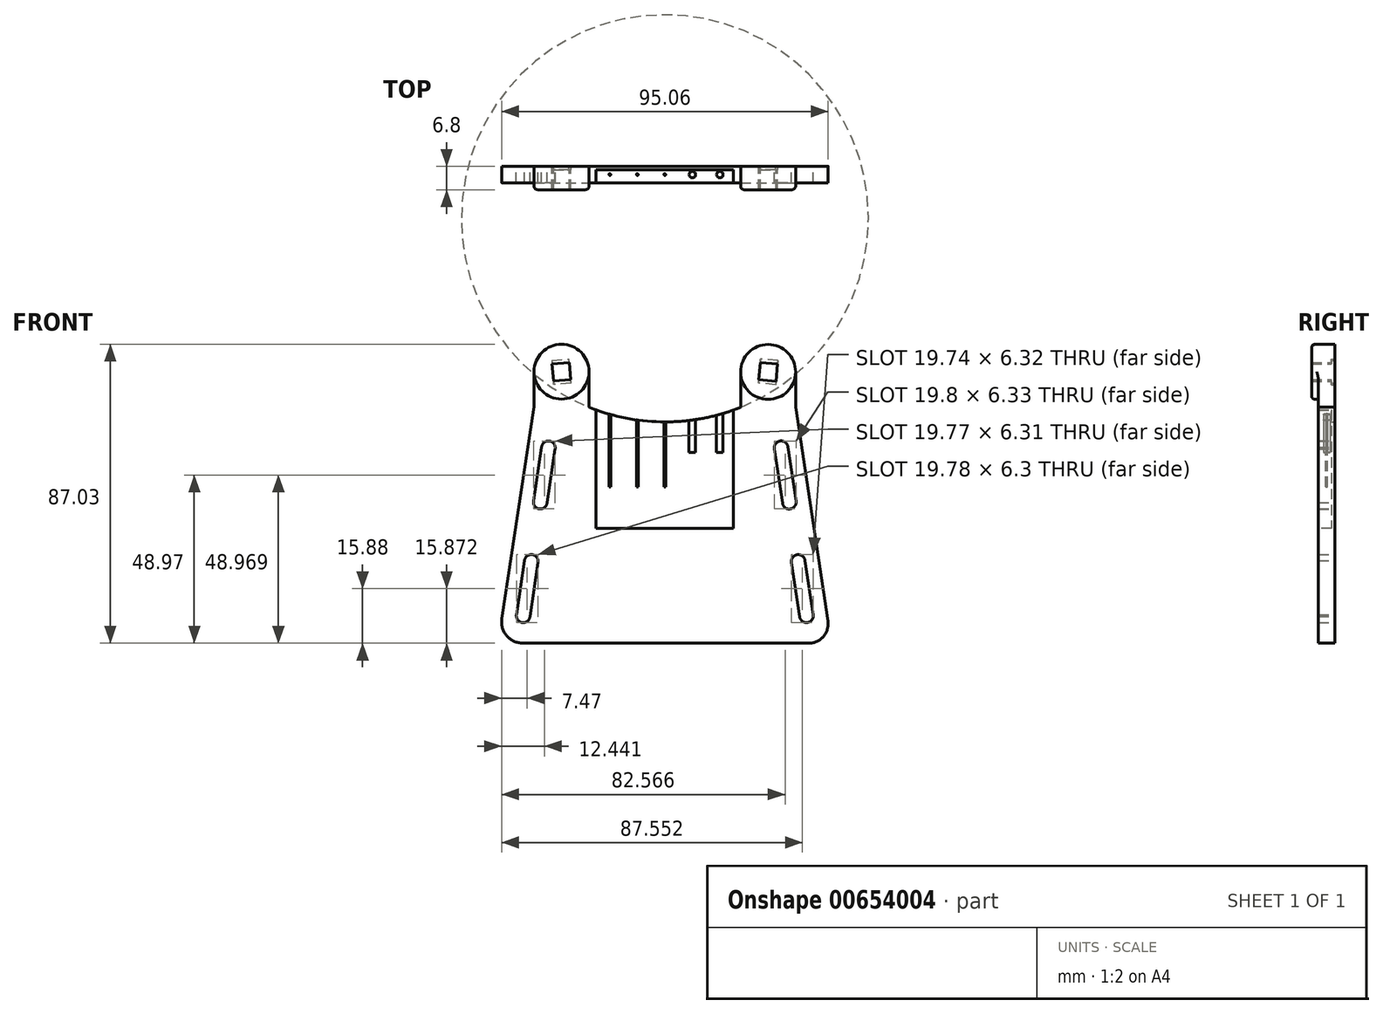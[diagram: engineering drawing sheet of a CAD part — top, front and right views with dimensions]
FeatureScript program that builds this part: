
annotation { "Feature Type Name" : "Feature", "Feature Type Description" : "" }
export const myFeature = defineFeature(function(context is Context, id is Id, definition is map)
    precondition{}
    {
        {
            assignVariable(context, id + "F0", {"name" : "thickness", "anyValue" : 4.8});
        }
        {
            var Q0;
            Q0=qCreatedBy(makeId("Front.planeOp"),FACE);
            var sketch = newSketch(context, id + "F1", { "sketchPlane" : qUnion([Q0])});
            skLineSegment(sketch, "E0", {"start": v(-22.08, 35.56) * mm, "end": v(-22.08, 25.22) * mm});
            skLineSegment(sketch, "E1", {"start": v(-38.08, 35.56) * mm, "end": v(-38.08, 25.41) * mm});
            skLineSegment(sketch, "E2", {"start": v(-38.08, 25.41) * mm, "end": v(-47.46, -36.38) * mm});
            skLineSegment(sketch, "E3", {"start": v(-41.37, -43.47) * mm, "end": v(41.96, -43.47) * mm});
            skLineSegment(sketch, "E4", {"start": v(47.46, -37.08) * mm, "end": v(38.06, 25.2) * mm});
            skLineSegment(sketch, "E5", {"start": v(38.06, 25.2) * mm, "end": v(38.06, 35.5) * mm});
            skLineSegment(sketch, "E6", {"start": v(22.06, 35.5) * mm, "end": v(22.06, 25.2) * mm});
            skArc(sketch, "E7", {"start": v(-22.08, 25.22) * mm, "mid": v(0, 20.95) * mm, "end": v(22.06, 25.2) * mm});
            skCircle(sketch, "E8", {"center": v(-30.08, 35.56) * mm, "radius": 8 * mm});
            skPoint(sketch, "E8.first.point", {"position": v(-30.38, 43.56) * mm});
            skCircle(sketch, "E9", {"center": v(30.06, 35.5) * mm, "radius": 8 * mm});
            skPoint(sketch, "E9.second.point", {"position": v(29.54, 43.49) * mm});
            skArc(sketch, "E10", {"start": v(47.46, -37.08) * mm, "mid": v(46.18, -41.54) * mm, "end": v(41.96, -43.47) * mm});
            skArc(sketch, "E11", {"start": v(-47.46, -36.38) * mm, "mid": v(-46.04, -41.33) * mm, "end": v(-41.37, -43.47) * mm});
            skLineSegment(sketch, "E12", {"start": v(0, 64.8) * mm, "end": v(0, 20.95) * mm, "construction": true});
            skLineSegment(sketch, "E13", {"start": v(0, 20.95) * mm, "end": v(0, -58.54) * mm, "construction": true});
            skLineSegment(sketch, "E14", {"start": v(-32.91, 38.84) * mm, "end": v(-32.4, 32.86) * mm});
            skLineSegment(sketch, "E15", {"start": v(-32.4, 32.86) * mm, "end": v(-27.37, 33.28) * mm});
            skLineSegment(sketch, "E16", {"start": v(-27.3, 32.29) * mm, "end": v(-27.88, 39.26) * mm});
            skLineSegment(sketch, "E17", {"start": v(-27.8, 38.26) * mm, "end": v(-32.83, 37.84) * mm});
            skLineSegment(sketch, "E18", {"start": v(27.8, 38.27) * mm, "end": v(32.83, 37.81) * mm});
            skLineSegment(sketch, "E19", {"start": v(32.83, 37.81) * mm, "end": v(32.38, 32.79) * mm});
            skLineSegment(sketch, "E20", {"start": v(32.38, 32.79) * mm, "end": v(27.35, 33.24) * mm});
            skLineSegment(sketch, "E21", {"start": v(27.35, 33.24) * mm, "end": v(27.8, 38.27) * mm});
            skCircle(sketch, "E22", {"center": v(-38.89, -19.68) * mm, "radius": 2 * mm});
            skPoint(sketch, "E22.first.point", {"position": v(-40.87, -19.42) * mm});
            skPoint(sketch, "E22.second.point", {"position": v(-38.56, -17.7) * mm});
            skPoint(sketch, "E22.third.point", {"position": v(-36.9, -19.96) * mm});
            skCircle(sketch, "E23", {"center": v(-33.9, 13.4) * mm, "radius": 2 * mm});
            skPoint(sketch, "E23.first.point", {"position": v(-35.87, 13.78) * mm});
            skPoint(sketch, "E23.second.point", {"position": v(-33.6, 15.38) * mm});
            skPoint(sketch, "E23.third.point", {"position": v(-31.92, 13.15) * mm});
            skLineSegment(sketch, "E24", {"start": v(-38.89, -19.68) * mm, "end": v(-42.46, -43.38) * mm, "construction": true});
            skCircle(sketch, "E25", {"center": v(-36.27, -2.4) * mm, "radius": 2 * mm});
            skPoint(sketch, "E25.first.point", {"position": v(-38.24, -2.1) * mm});
            skPoint(sketch, "E25.second.point", {"position": v(-36.46, -4.39) * mm});
            skPoint(sketch, "E25.third.point", {"position": v(-34.31, -2.83) * mm});
            skCircle(sketch, "E26", {"center": v(33.85, 13.42) * mm, "radius": 2 * mm});
            skPoint(sketch, "E26.first.point", {"position": v(31.87, 13.12) * mm});
            skPoint(sketch, "E26.second.point", {"position": v(33.41, 15.37) * mm});
            skPoint(sketch, "E26.third.point", {"position": v(35.83, 13.72) * mm});
            skCircle(sketch, "E27", {"center": v(36.22, -2.42) * mm, "radius": 2 * mm});
            skPoint(sketch, "E27.first.point", {"position": v(34.24, -2.72) * mm});
            skPoint(sketch, "E27.second.point", {"position": v(38.2, -2.13) * mm});
            skPoint(sketch, "E27.third.point", {"position": v(36.66, -4.37) * mm});
            skCircle(sketch, "E28", {"center": v(38.84, -19.7) * mm, "radius": 2 * mm});
            skPoint(sketch, "E28.first.point", {"position": v(36.86, -20) * mm});
            skPoint(sketch, "E28.second.point", {"position": v(38.61, -17.72) * mm});
            skPoint(sketch, "E28.third.point", {"position": v(40.82, -19.4) * mm});
            skLineSegment(sketch, "E29", {"start": v(42.42, -43.46) * mm, "end": v(29.32, 43.47) * mm, "construction": true});
            skLineSegment(sketch, "E30", {"start": v(-27.3, 32.29) * mm, "end": v(-32.32, 31.86) * mm});
            skLineSegment(sketch, "E31", {"start": v(-32.32, 31.86) * mm, "end": v(-32.4, 32.86) * mm});
            skLineSegment(sketch, "E32", {"start": v(-32.91, 38.84) * mm, "end": v(-27.88, 39.26) * mm});
            skLineSegment(sketch, "E33", {"start": v(32.83, 37.81) * mm, "end": v(32.92, 38.81) * mm});
            skLineSegment(sketch, "E34", {"start": v(32.92, 38.81) * mm, "end": v(27.89, 39.26) * mm});
            skLineSegment(sketch, "E35", {"start": v(27.89, 39.26) * mm, "end": v(27.8, 38.27) * mm});
            skLineSegment(sketch, "E36", {"start": v(32.38, 32.79) * mm, "end": v(32.29, 31.8) * mm});
            skLineSegment(sketch, "E37", {"start": v(32.29, 31.8) * mm, "end": v(27.26, 32.24) * mm});
            skLineSegment(sketch, "E38", {"start": v(27.26, 32.24) * mm, "end": v(27.35, 33.24) * mm});
            skCircle(sketch, "E39", {"center": v(-41.24, -35.5) * mm, "radius": 2 * mm});
            skPoint(sketch, "E39.first.point", {"position": v(-43.2, -35.2) * mm});
            skPoint(sketch, "E39.second.point", {"position": v(-41.57, -37.47) * mm});
            skPoint(sketch, "E39.third.point", {"position": v(-39.27, -35.84) * mm});
            skCircle(sketch, "E40", {"center": v(41.23, -35.5) * mm, "radius": 1.99 * mm});
            skPoint(sketch, "E40.first.point", {"position": v(39.26, -35.8) * mm});
            skPoint(sketch, "E40.second.point", {"position": v(41.52, -37.47) * mm});
            skPoint(sketch, "E40.third.point", {"position": v(43.2, -35.29) * mm});
            skLineSegment(sketch, "E41", {"start": v(35.83, 13.72) * mm, "end": v(38.2, -2.13) * mm});
            skLineSegment(sketch, "E42", {"start": v(31.87, 13.12) * mm, "end": v(34.24, -2.72) * mm});
            skLineSegment(sketch, "E43", {"start": v(36.86, -20) * mm, "end": v(39.26, -35.8) * mm});
            skLineSegment(sketch, "E44", {"start": v(40.82, -19.4) * mm, "end": v(43.2, -35.29) * mm});
            skLineSegment(sketch, "E45", {"start": v(-40.87, -19.42) * mm, "end": v(-43.2, -35.2) * mm});
            skLineSegment(sketch, "E46", {"start": v(-36.9, -19.96) * mm, "end": v(-39.27, -35.84) * mm});
            skLineSegment(sketch, "E47", {"start": v(-35.87, 13.78) * mm, "end": v(-38.24, -2.1) * mm});
            skLineSegment(sketch, "E48", {"start": v(-31.92, 13.15) * mm, "end": v(-34.31, -2.83) * mm});
            skSolve(sketch);
        }
        {
            var Q0;
            {var subQ20=sQuery(id+"F1.wireOp",EDGE,"E0");Q0=makeQuery(id+"F1.imprint","IMPRINT",FACE,{"disambiguationData":[TD([[makeQuery(id+"F1.imprint","IMPRINT",EDGE,{"derivedFrom":subQ20}),-1.0]])]});}
            var Q1;
            {var subQ12=sQuery(id+"F1.wireOp",EDGE,"E30");Q1=makeQuery(id+"F1.imprint","IMPRINT",FACE,{"disambiguationData":[TD([[makeQuery(id+"F1.imprint","IMPRINT",EDGE,{"derivedFrom":subQ12}),1.0]])]});}
            var Q2;
            Q2=makeQuery(id+"F1.imprint","IMPRINT",FACE,{"disambiguationData":[TD([[makeQuery(id+"F1.imprint","IMPRINT",EDGE,{"derivedFrom":sQuery(id+"F1.wireOp",EDGE,"E19")}),1.0]])]});
            var Q3;
            {var subQ0=sQuery(id+"F1.wireOp",EDGE,"E15");Q3=makeQuery(id+"F1.imprint","IMPRINT",FACE,{"disambiguationData":[TD([[makeQuery(id+"F1.imprint","IMPRINT",EDGE,{"derivedFrom":subQ0}),-1.0]])]});}
            var Q4;
            {var subQ2=sQuery(id+"F1.wireOp",EDGE,"E17");Q4=makeQuery(id+"F1.imprint","IMPRINT",FACE,{"disambiguationData":[TD([[makeQuery(id+"F1.imprint","IMPRINT",EDGE,{"derivedFrom":subQ2}),-1.0]])]});}
            var Q5;
            Q5=makeQuery(id+"F1.imprint","IMPRINT",FACE,{"disambiguationData":[TD([[makeQuery(id+"F1.imprint","IMPRINT",EDGE,{"derivedFrom":sQuery(id+"F1.wireOp",EDGE,"E20")}),1.0]])]});
            var Q6;
            Q6=makeQuery(id+"F1.imprint","IMPRINT",FACE,{"disambiguationData":[TD([[makeQuery(id+"F1.imprint","IMPRINT",EDGE,{"derivedFrom":sQuery(id+"F1.wireOp",EDGE,"E18")}),1.0]])]});
            extrude(context, id + "F2", {"entities" : qUnion([Q0, Q1, Q2, Q3, Q4, Q5, Q6]), "depth" : (getVariable(context, 'thickness')) * mm, "offsetDistance" : 25 * mm});
        }
        {
            var Q0;
            {var subQ12=sQuery(id+"F1.wireOp",EDGE,"E30");Q0=makeQuery(id+"F1.imprint","IMPRINT",FACE,{"disambiguationData":[TD([[makeQuery(id+"F1.imprint","IMPRINT",EDGE,{"derivedFrom":subQ12}),1.0]])]});}
            var Q1;
            Q1=makeQuery(id+"F1.imprint","IMPRINT",FACE,{"disambiguationData":[TD([[makeQuery(id+"F1.imprint","IMPRINT",EDGE,{"derivedFrom":sQuery(id+"F1.wireOp",EDGE,"E19")}),1.0]])]});
            var Q2;
            Q2=makeQuery(id+"F1.imprint","IMPRINT",FACE,{"disambiguationData":[TD([[makeQuery(id+"F1.imprint","IMPRINT",EDGE,{"derivedFrom":sQuery(id+"F1.wireOp",EDGE,"E20")}),1.0]])]});
            var Q3;
            Q3=makeQuery(id+"F1.imprint","IMPRINT",FACE,{"disambiguationData":[TD([[makeQuery(id+"F1.imprint","IMPRINT",EDGE,{"derivedFrom":sQuery(id+"F1.wireOp",EDGE,"E18")}),1.0]])]});
            var Q4;
            {var subQ0=sQuery(id+"F1.wireOp",EDGE,"E15");Q4=makeQuery(id+"F1.imprint","IMPRINT",FACE,{"disambiguationData":[TD([[makeQuery(id+"F1.imprint","IMPRINT",EDGE,{"derivedFrom":subQ0}),-1.0]])]});}
            var Q5;
            {var subQ2=sQuery(id+"F1.wireOp",EDGE,"E17");Q5=makeQuery(id+"F1.imprint","IMPRINT",FACE,{"disambiguationData":[TD([[makeQuery(id+"F1.imprint","IMPRINT",EDGE,{"derivedFrom":subQ2}),-1.0]])]});}
            extrude(context, id + "F3", {"entities" : qUnion([Q0, Q1, Q2, Q3, Q4, Q5]), "operationType" : NewBodyOperationType.ADD, "depth" : (getVariable(context, 'thickness') + 2) * mm, "offsetDistance" : 25 * mm});
        }
        {
            var Q0;
            Q0=makeQuery(id+"F3.opExtrude","CAP_EDGE",EDGE,{"disambiguationData":[OSD([sQuery(id+"F1.wireOp",EDGE,"E8")])],"isStart":false});
            var Q1;
            Q1=makeQuery(id+"F3.opExtrude","CAP_EDGE",EDGE,{"disambiguationData":[OSD([sQuery(id+"F1.wireOp",EDGE,"E9")])],"isStart":false});
            fillet(context, id + "F4", {"entities" : qUnion([Q0, Q1]), "radius" : 1 * mm, "tangentPropagation" : true, "allowEdgeOverflow" : false});
        }
        {
            var Q0;
            {var subQ0=sQuery(id+"F1.wireOp",EDGE,"E9");Q0=makeQuery(id+"F3.boolean.opBoolean","INTERSECT",EDGE,{"derivedFrom":[makeQuery(id+"F2.opExtrude","CAP_FACE",FACE,{"disambiguationData":[OSD([sQuery(id+"F1.wireOp",EDGE,"E0"),sQuery(id+"F1.wireOp",EDGE,"E1"),sQuery(id+"F1.wireOp",EDGE,"E2"),sQuery(id+"F1.wireOp",EDGE,"E3"),sQuery(id+"F1.wireOp",EDGE,"E4"),sQuery(id+"F1.wireOp",EDGE,"E5"),sQuery(id+"F1.wireOp",EDGE,"E6"),sQuery(id+"F1.wireOp",EDGE,"E7"),sQuery(id+"F1.wireOp",EDGE,"E8"),subQ0,sQuery(id+"F1.wireOp",EDGE,"E10"),sQuery(id+"F1.wireOp",EDGE,"E11"),sQuery(id+"F1.wireOp",EDGE,"E14"),sQuery(id+"F1.wireOp",EDGE,"E15"),sQuery(id+"F1.wireOp",EDGE,"E16"),sQuery(id+"F1.wireOp",EDGE,"E17"),sQuery(id+"F1.wireOp",EDGE,"E18"),sQuery(id+"F1.wireOp",EDGE,"E19"),sQuery(id+"F1.wireOp",EDGE,"E20"),sQuery(id+"F1.wireOp",EDGE,"E21"),sQuery(id+"F1.wireOp",EDGE,"E22"),sQuery(id+"F1.wireOp",EDGE,"E23"),sQuery(id+"F1.wireOp",EDGE,"E25"),sQuery(id+"F1.wireOp",EDGE,"E26"),sQuery(id+"F1.wireOp",EDGE,"E27"),sQuery(id+"F1.wireOp",EDGE,"E28"),sQuery(id+"F1.wireOp",EDGE,"E39"),sQuery(id+"F1.wireOp",EDGE,"E40"),sQuery(id+"F1.wireOp",EDGE,"E41"),sQuery(id+"F1.wireOp",EDGE,"E42"),sQuery(id+"F1.wireOp",EDGE,"E43"),sQuery(id+"F1.wireOp",EDGE,"E44"),sQuery(id+"F1.wireOp",EDGE,"E45"),sQuery(id+"F1.wireOp",EDGE,"E46"),sQuery(id+"F1.wireOp",EDGE,"E47"),sQuery(id+"F1.wireOp",EDGE,"E48")])],"isStart":false}),makeQuery(id+"F3.opExtrude","SWEPT_FACE",FACE,{"disambiguationData":[OSD([subQ0])]})]});}
            var Q1;
            {var subQ0=sQuery(id+"F1.wireOp",EDGE,"E8");Q1=makeQuery(id+"F3.boolean.opBoolean","INTERSECT",EDGE,{"derivedFrom":[makeQuery(id+"F2.opExtrude","CAP_FACE",FACE,{"disambiguationData":[OSD([sQuery(id+"F1.wireOp",EDGE,"E0"),sQuery(id+"F1.wireOp",EDGE,"E1"),sQuery(id+"F1.wireOp",EDGE,"E2"),sQuery(id+"F1.wireOp",EDGE,"E3"),sQuery(id+"F1.wireOp",EDGE,"E4"),sQuery(id+"F1.wireOp",EDGE,"E5"),sQuery(id+"F1.wireOp",EDGE,"E6"),sQuery(id+"F1.wireOp",EDGE,"E7"),subQ0,sQuery(id+"F1.wireOp",EDGE,"E9"),sQuery(id+"F1.wireOp",EDGE,"E10"),sQuery(id+"F1.wireOp",EDGE,"E11"),sQuery(id+"F1.wireOp",EDGE,"E14"),sQuery(id+"F1.wireOp",EDGE,"E15"),sQuery(id+"F1.wireOp",EDGE,"E16"),sQuery(id+"F1.wireOp",EDGE,"E17"),sQuery(id+"F1.wireOp",EDGE,"E18"),sQuery(id+"F1.wireOp",EDGE,"E19"),sQuery(id+"F1.wireOp",EDGE,"E20"),sQuery(id+"F1.wireOp",EDGE,"E21"),sQuery(id+"F1.wireOp",EDGE,"E22"),sQuery(id+"F1.wireOp",EDGE,"E23"),sQuery(id+"F1.wireOp",EDGE,"E25"),sQuery(id+"F1.wireOp",EDGE,"E26"),sQuery(id+"F1.wireOp",EDGE,"E27"),sQuery(id+"F1.wireOp",EDGE,"E28"),sQuery(id+"F1.wireOp",EDGE,"E39"),sQuery(id+"F1.wireOp",EDGE,"E40"),sQuery(id+"F1.wireOp",EDGE,"E41"),sQuery(id+"F1.wireOp",EDGE,"E42"),sQuery(id+"F1.wireOp",EDGE,"E43"),sQuery(id+"F1.wireOp",EDGE,"E44"),sQuery(id+"F1.wireOp",EDGE,"E45"),sQuery(id+"F1.wireOp",EDGE,"E46"),sQuery(id+"F1.wireOp",EDGE,"E47"),sQuery(id+"F1.wireOp",EDGE,"E48")])],"isStart":false}),makeQuery(id+"F3.opExtrude","SWEPT_FACE",FACE,{"disambiguationData":[OSD([subQ0])]})]});}
            fillet(context, id + "F5", {"entities" : qUnion([Q0, Q1]), "radius" : 0.5 * mm, "tangentPropagation" : true, "allowEdgeOverflow" : false});
        }
        {
            var Q0;
            Q0=makeQuery(id+"F2.opExtrude","CAP_FACE",FACE,{"disambiguationData":[OSD([sQuery(id+"F1.wireOp",EDGE,"E0"),sQuery(id+"F1.wireOp",EDGE,"E1"),sQuery(id+"F1.wireOp",EDGE,"E2"),sQuery(id+"F1.wireOp",EDGE,"E3"),sQuery(id+"F1.wireOp",EDGE,"E4"),sQuery(id+"F1.wireOp",EDGE,"E5"),sQuery(id+"F1.wireOp",EDGE,"E6"),sQuery(id+"F1.wireOp",EDGE,"E7"),sQuery(id+"F1.wireOp",EDGE,"E8"),sQuery(id+"F1.wireOp",EDGE,"E9"),sQuery(id+"F1.wireOp",EDGE,"E10"),sQuery(id+"F1.wireOp",EDGE,"E11"),sQuery(id+"F1.wireOp",EDGE,"E14"),sQuery(id+"F1.wireOp",EDGE,"E15"),sQuery(id+"F1.wireOp",EDGE,"E16"),sQuery(id+"F1.wireOp",EDGE,"E17"),sQuery(id+"F1.wireOp",EDGE,"E18"),sQuery(id+"F1.wireOp",EDGE,"E19"),sQuery(id+"F1.wireOp",EDGE,"E20"),sQuery(id+"F1.wireOp",EDGE,"E21"),sQuery(id+"F1.wireOp",EDGE,"E22"),sQuery(id+"F1.wireOp",EDGE,"E23"),sQuery(id+"F1.wireOp",EDGE,"E25"),sQuery(id+"F1.wireOp",EDGE,"E26"),sQuery(id+"F1.wireOp",EDGE,"E27"),sQuery(id+"F1.wireOp",EDGE,"E28"),sQuery(id+"F1.wireOp",EDGE,"E39"),sQuery(id+"F1.wireOp",EDGE,"E40"),sQuery(id+"F1.wireOp",EDGE,"E41"),sQuery(id+"F1.wireOp",EDGE,"E42"),sQuery(id+"F1.wireOp",EDGE,"E43"),sQuery(id+"F1.wireOp",EDGE,"E44"),sQuery(id+"F1.wireOp",EDGE,"E45"),sQuery(id+"F1.wireOp",EDGE,"E46"),sQuery(id+"F1.wireOp",EDGE,"E47"),sQuery(id+"F1.wireOp",EDGE,"E48")])],"isStart":false});
            var sketch = newSketch(context, id + "F6", { "sketchPlane" : qUnion([Q0])});
            skLineSegment(sketch, "E49", {"start": v(0, 12) * mm, "end": v(-20, 12) * mm});
            skLineSegment(sketch, "E50", {"start": v(-20, 12) * mm, "end": v(-20, -10) * mm});
            skLineSegment(sketch, "E51", {"start": v(-20, -10) * mm, "end": v(0, -10) * mm});
            skLineSegment(sketch, "E52.MirrorCS", {"start": v(-20, 12) * mm, "end": v(-20, 34) * mm});
            skLineSegment(sketch, "E53.MirrorCS", {"start": v(-20, 34) * mm, "end": v(0, 34) * mm});
            skLineSegment(sketch, "E54.MirrorCS", {"start": v(0, 12) * mm, "end": v(20, 12) * mm});
            skLineSegment(sketch, "E55.MirrorCS", {"start": v(20, 12) * mm, "end": v(20, -10) * mm});
            skLineSegment(sketch, "E56.MirrorCS", {"start": v(20, -10) * mm, "end": v(0, -10) * mm});
            skSolve(sketch);
        }
        {
            var Q0;
            Q0=makeQuery(id+"F6.imprint","IMPRINT",FACE,{"disambiguationData":[TD([[makeQuery(id+"F6.imprint","IMPRINT",EDGE,{"derivedFrom":sQuery(id+"F6.wireOp",EDGE,"E49")}),1.0]])]});
            extrude(context, id + "F7", {"entities" : qUnion([Q0]), "operationType" : NewBodyOperationType.REMOVE, "oppositeDirection" : true, "depth" : (getVariable(context, 'thickness') - 1) * mm, "offsetDistance" : 25 * mm});
        }
        {
            var Q0;
            {var subQ0=sQuery(id+"F1.wireOp",EDGE,"E15");Q0=makeQuery(id+"F1.imprint","IMPRINT",FACE,{"disambiguationData":[TD([[makeQuery(id+"F1.imprint","IMPRINT",EDGE,{"derivedFrom":subQ0}),-1.0]])]});}
            var Q1;
            {var subQ2=sQuery(id+"F1.wireOp",EDGE,"E17");Q1=makeQuery(id+"F1.imprint","IMPRINT",FACE,{"disambiguationData":[TD([[makeQuery(id+"F1.imprint","IMPRINT",EDGE,{"derivedFrom":subQ2}),-1.0]])]});}
            var Q2;
            Q2=makeQuery(id+"F1.imprint","IMPRINT",FACE,{"disambiguationData":[TD([[makeQuery(id+"F1.imprint","IMPRINT",EDGE,{"derivedFrom":sQuery(id+"F1.wireOp",EDGE,"E20")}),1.0]])]});
            var Q3;
            Q3=makeQuery(id+"F1.imprint","IMPRINT",FACE,{"disambiguationData":[TD([[makeQuery(id+"F1.imprint","IMPRINT",EDGE,{"derivedFrom":sQuery(id+"F1.wireOp",EDGE,"E18")}),1.0]])]});
            extrude(context, id + "F8", {"entities" : qUnion([Q0, Q1, Q2, Q3]), "operationType" : NewBodyOperationType.REMOVE, "depth" : 1 * mm, "offsetDistance" : 25 * mm});
        }
        {
            var Q0;
            Q0=makeQuery(id+"F7.boolean.opBoolean","COPY",FACE,{"derivedFrom":makeQuery(id+"F7.opExtrude","SWEPT_FACE",FACE,{"disambiguationData":[OSD([sQuery(id+"F6.wireOp",EDGE,"E49"),sQuery(id+"F6.wireOp",EDGE,"E54.MirrorCS")])]})});
            var sketch = newSketch(context, id + "F9", { "sketchPlane" : qUnion([Q0])});
            skCircle(sketch, "E57", {"center": v(0, 2.4) * mm, "radius": 0.95 * mm});
            skCircle(sketch, "E58", {"center": v(-8, 2.4) * mm, "radius": 0.95 * mm});
            skCircle(sketch, "E59", {"center": v(-16, 2.4) * mm, "radius": 0.95 * mm});
            skCircle(sketch, "E60.MirrorC", {"center": v(8, 2.4) * mm, "radius": 0.95 * mm});
            skCircle(sketch, "E61.MirrorC", {"center": v(16, 2.4) * mm, "radius": 0.95 * mm});
            skCircle(sketch, "E62", {"center": v(-16, 2.4) * mm, "radius": 0.25 * mm});
            skCircle(sketch, "E63", {"center": v(-8, 2.4) * mm, "radius": 0.25 * mm});
            skCircle(sketch, "E64", {"center": v(0, 2.4) * mm, "radius": 0.25 * mm});
            skCircle(sketch, "E65", {"center": v(8, 2.4) * mm, "radius": 0.25 * mm});
            skCircle(sketch, "E66", {"center": v(16, 2.4) * mm, "radius": 0.25 * mm});
            skSolve(sketch);
        }
        {
            var Q0;
            Q0=makeQuery(id+"F9.imprint","IMPRINT",FACE,{"disambiguationData":[TD([[makeQuery(id+"F9.imprint","IMPRINT",EDGE,{"derivedFrom":sQuery(id+"F9.wireOp",EDGE,"E59")}),1.0]])]});
            var Q1;
            Q1=makeQuery(id+"F9.imprint","IMPRINT",FACE,{"disambiguationData":[TD([[makeQuery(id+"F9.imprint","IMPRINT",EDGE,{"derivedFrom":sQuery(id+"F9.wireOp",EDGE,"E58")}),1.0]])]});
            var Q2;
            Q2=makeQuery(id+"F9.imprint","IMPRINT",FACE,{"disambiguationData":[TD([[makeQuery(id+"F9.imprint","IMPRINT",EDGE,{"derivedFrom":sQuery(id+"F9.wireOp",EDGE,"E57")}),1.0]])]});
            var Q3;
            Q3=makeQuery(id+"F9.imprint","IMPRINT",FACE,{"disambiguationData":[TD([[makeQuery(id+"F9.imprint","IMPRINT",EDGE,{"derivedFrom":sQuery(id+"F9.wireOp",EDGE,"E60.MirrorC")}),-1.0]])]});
            var Q4;
            Q4=makeQuery(id+"F9.imprint","IMPRINT",FACE,{"disambiguationData":[TD([[makeQuery(id+"F9.imprint","IMPRINT",EDGE,{"derivedFrom":sQuery(id+"F9.wireOp",EDGE,"E61.MirrorC")}),-1.0]])]});
            extrude(context, id + "F10", {"entities" : qUnion([Q0, Q1, Q2, Q3, Q4]), "operationType" : NewBodyOperationType.REMOVE, "oppositeDirection" : true, "depth" : 25 * mm, "offsetDistance" : 25 * mm});
        }
        {
            var Q0;
            Q0=makeQuery(id+"F10.boolean.opBoolean","SPLIT",FACE,{"disambiguationData":[TD([makeQuery(id+"F10.opExtrude","SWEPT_FACE",FACE,{"disambiguationData":[OSD([sQuery(id+"F9.wireOp",EDGE,"E66")])]})])],"derivedFrom":makeQuery(id+"F7.boolean.opBoolean","COPY",FACE,{"derivedFrom":makeQuery(id+"F7.opExtrude","SWEPT_FACE",FACE,{"disambiguationData":[OSD([sQuery(id+"F6.wireOp",EDGE,"E49"),sQuery(id+"F6.wireOp",EDGE,"E54.MirrorCS")])]})})});
            var Q1;
            Q1=makeQuery(id+"F10.boolean.opBoolean","SPLIT",FACE,{"disambiguationData":[TD([makeQuery(id+"F10.opExtrude","SWEPT_FACE",FACE,{"disambiguationData":[OSD([sQuery(id+"F9.wireOp",EDGE,"E65")])]})])],"derivedFrom":makeQuery(id+"F7.boolean.opBoolean","COPY",FACE,{"derivedFrom":makeQuery(id+"F7.opExtrude","SWEPT_FACE",FACE,{"disambiguationData":[OSD([sQuery(id+"F6.wireOp",EDGE,"E49"),sQuery(id+"F6.wireOp",EDGE,"E54.MirrorCS")])]})})});
            var Q2;
            Q2=makeQuery(id+"F10.boolean.opBoolean","SPLIT",FACE,{"disambiguationData":[TD([makeQuery(id+"F10.opExtrude","SWEPT_FACE",FACE,{"disambiguationData":[OSD([sQuery(id+"F9.wireOp",EDGE,"E64")])]})])],"derivedFrom":makeQuery(id+"F7.boolean.opBoolean","COPY",FACE,{"derivedFrom":makeQuery(id+"F7.opExtrude","SWEPT_FACE",FACE,{"disambiguationData":[OSD([sQuery(id+"F6.wireOp",EDGE,"E49"),sQuery(id+"F6.wireOp",EDGE,"E54.MirrorCS")])]})})});
            var Q3;
            Q3=makeQuery(id+"F10.boolean.opBoolean","SPLIT",FACE,{"disambiguationData":[TD([makeQuery(id+"F10.opExtrude","SWEPT_FACE",FACE,{"disambiguationData":[OSD([sQuery(id+"F9.wireOp",EDGE,"E62")])]})])],"derivedFrom":makeQuery(id+"F7.boolean.opBoolean","COPY",FACE,{"derivedFrom":makeQuery(id+"F7.opExtrude","SWEPT_FACE",FACE,{"disambiguationData":[OSD([sQuery(id+"F6.wireOp",EDGE,"E49"),sQuery(id+"F6.wireOp",EDGE,"E54.MirrorCS")])]})})});
            var Q4;
            Q4=makeQuery(id+"F10.boolean.opBoolean","SPLIT",FACE,{"disambiguationData":[TD([makeQuery(id+"F10.opExtrude","SWEPT_FACE",FACE,{"disambiguationData":[OSD([sQuery(id+"F9.wireOp",EDGE,"E63")])]})])],"derivedFrom":makeQuery(id+"F7.boolean.opBoolean","COPY",FACE,{"derivedFrom":makeQuery(id+"F7.opExtrude","SWEPT_FACE",FACE,{"disambiguationData":[OSD([sQuery(id+"F6.wireOp",EDGE,"E49"),sQuery(id+"F6.wireOp",EDGE,"E54.MirrorCS")])]})})});
            extrude(context, id + "F11", {"entities" : qUnion([Q0, Q1, Q2, Q3, Q4]), "depth" : 10 * mm, "offsetDistance" : 25 * mm});
        }
    });
